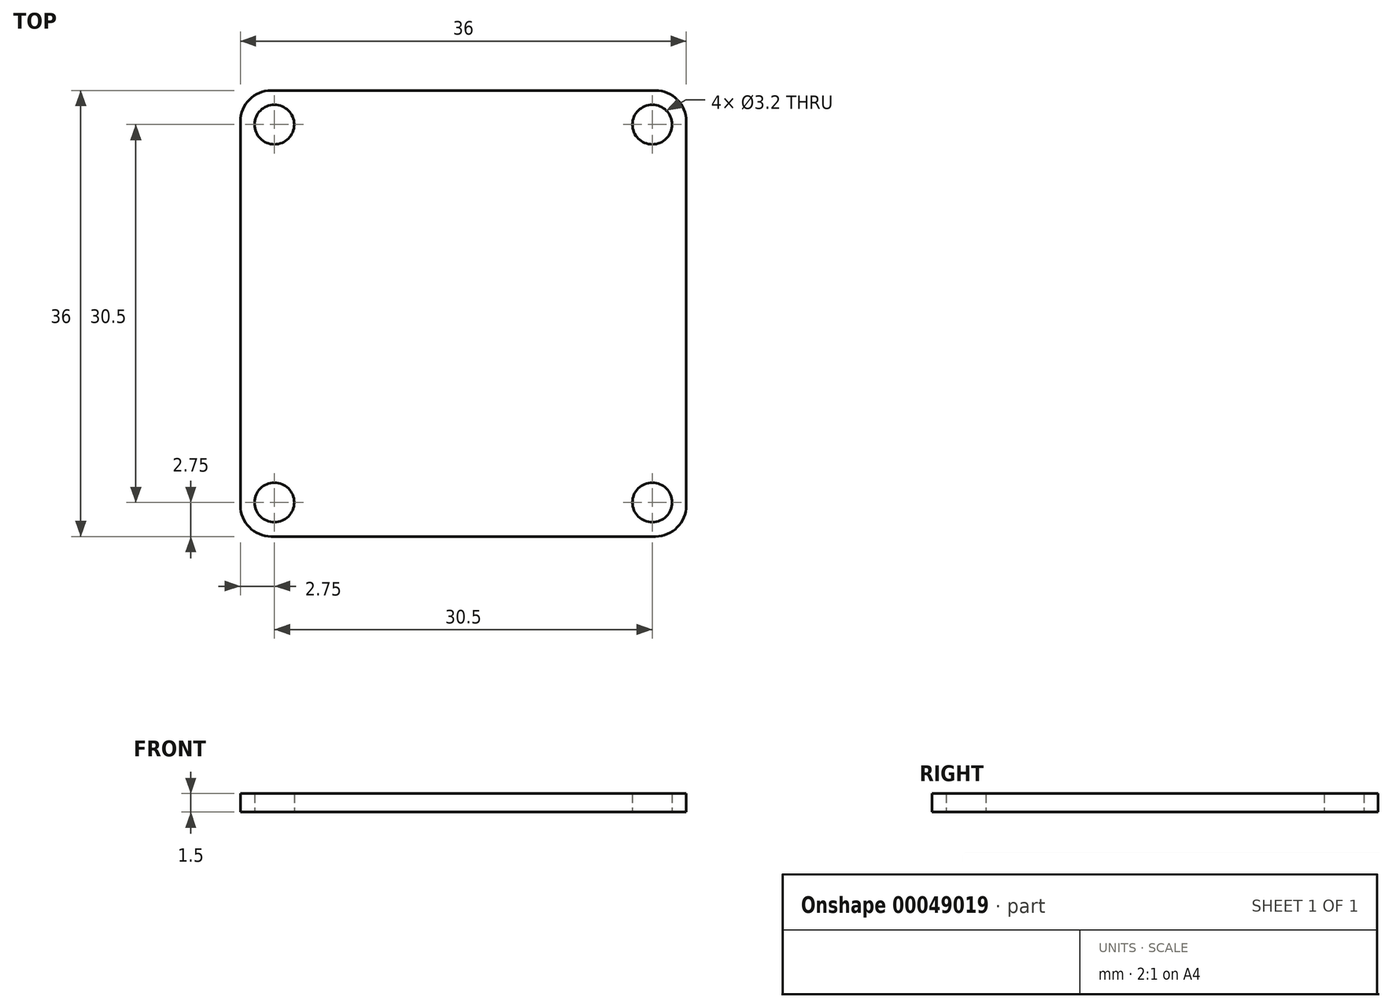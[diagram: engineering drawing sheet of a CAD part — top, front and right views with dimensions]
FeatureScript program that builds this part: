
annotation { "Feature Type Name" : "Feature", "Feature Type Description" : "" }
export const myFeature = defineFeature(function(context is Context, id is Id, definition is map)
    precondition{}
    {
        {
            var Q0;
            Q0=qCreatedBy(makeId("Top.planeOp"),FACE);
            var sketch = newSketch(context, id + "F0", { "sketchPlane" : qUnion([Q0])});
            skLineSegment(sketch, "E0.bottom", {"start": v(15.5, 18) * mm, "end": v(-15.5, 18) * mm});
            skLineSegment(sketch, "E0.top", {"start": v(15.5, -18) * mm, "end": v(-15.5, -18) * mm});
            skLineSegment(sketch, "E0.left", {"start": v(18, 15.5) * mm, "end": v(18, -15.5) * mm});
            skLineSegment(sketch, "E0.right", {"start": v(-18, 15.5) * mm, "end": v(-18, -15.5) * mm});
            skPoint(sketch, "E0.middle", {"position": v(0, 0) * mm});
            skPoint(sketch, "E1.visualSharp", {"position": v(-18, 18) * mm});
            skArc(sketch, "E1.filletArc", {"start": v(-15.5, 18) * mm, "mid": v(-17.27, 17.27) * mm, "end": v(-18, 15.5) * mm});
            skPoint(sketch, "E2.visualSharp", {"position": v(18, 18) * mm});
            skArc(sketch, "E2.filletArc", {"start": v(18, 15.5) * mm, "mid": v(17.27, 17.27) * mm, "end": v(15.5, 18) * mm});
            skPoint(sketch, "E3.visualSharp", {"position": v(18, -18) * mm});
            skArc(sketch, "E3.filletArc", {"start": v(15.5, -18) * mm, "mid": v(17.27, -17.27) * mm, "end": v(18, -15.5) * mm});
            skPoint(sketch, "E4.visualSharp", {"position": v(-18, -18) * mm});
            skArc(sketch, "E4.filletArc", {"start": v(-18, -15.5) * mm, "mid": v(-17.27, -17.27) * mm, "end": v(-15.5, -18) * mm});
            skLineSegment(sketch, "E5", {"start": v(0, 0) * mm, "end": v(18, 18) * mm, "construction": true});
            skLineSegment(sketch, "E6", {"start": v(0, 0) * mm, "end": v(-18, 18) * mm, "construction": true});
            skCircle(sketch, "E7", {"center": v(15.25, 15.25) * mm, "radius": 1.6 * mm});
            skCircle(sketch, "E8.1.0", {"center": v(15.25, -15.25) * mm, "radius": 1.6 * mm});
            skCircle(sketch, "E8.2.0", {"center": v(-15.25, -15.25) * mm, "radius": 1.6 * mm});
            skCircle(sketch, "E8.3.0", {"center": v(-15.25, 15.25) * mm, "radius": 1.6 * mm});
            skLineSegment(sketch, "E8.anchor1", {"start": v(0, 0) * mm, "end": v(15.25, 15.25) * mm, "construction": true});
            skLineSegment(sketch, "E8.anchor2", {"start": v(0, 0) * mm, "end": v(-15.25, 15.25) * mm, "construction": true});
            skSolve(sketch);
        }
        {
            var Q0;
            Q0=qSketchRegion(id+"F0",true);
            extrude(context, id + "F1", {"entities" : qUnion([Q0]), "depth" : 1.5 * mm});
        }
    });
